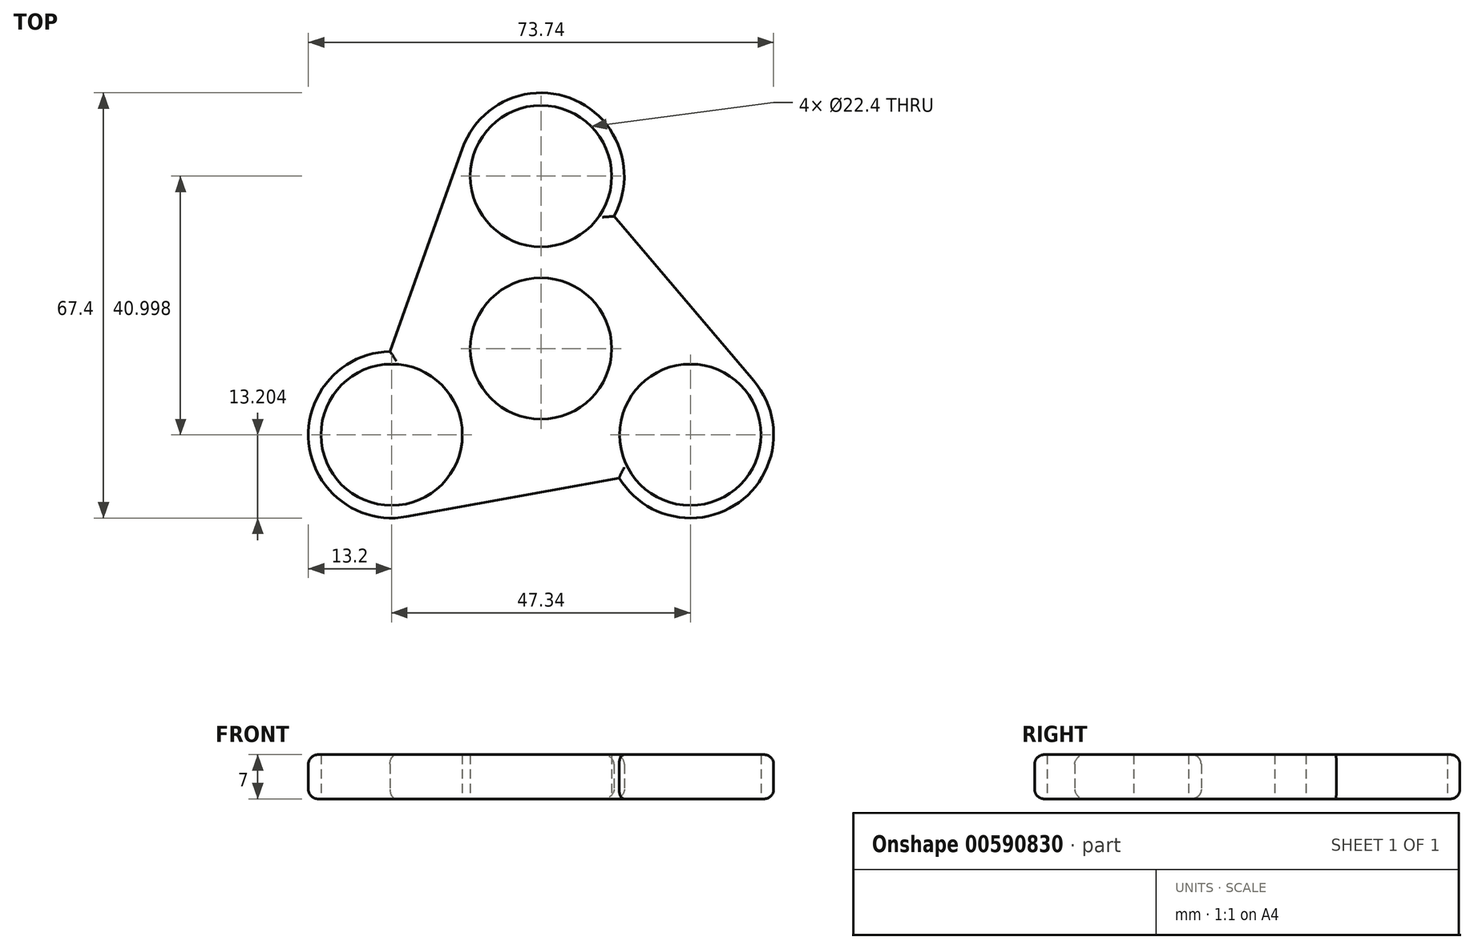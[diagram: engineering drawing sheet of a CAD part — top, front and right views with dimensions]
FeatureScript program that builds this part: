
annotation { "Feature Type Name" : "Feature", "Feature Type Description" : "" }
export const myFeature = defineFeature(function(context is Context, id is Id, definition is map)
    precondition{}
    {
        {
            var Q0;
            Q0=qCreatedBy(makeId("Top.planeOp"),FACE);
            var sketch = newSketch(context, id + "F0", { "sketchPlane" : qUnion([Q0])});
            skCircle(sketch, "E0", {"center": v(0, 0) * mm, "radius": 11.2 * mm});
            skCircle(sketch, "E1", {"center": v(0, 27.33) * mm, "radius": 11.2 * mm});
            skArc(sketch, "E2", {"start": v(11.57, 20.97) * mm, "mid": v(5.42, 39.37) * mm, "end": v(-12.43, 31.77) * mm});
            skCircle(sketch, "E3.1.0", {"center": v(-23.67, -13.67) * mm, "radius": 11.2 * mm});
            skArc(sketch, "E3.1.1", {"start": v(-23.95, -0.47) * mm, "mid": v(-36.8, -15) * mm, "end": v(-21.3, -26.65) * mm});
            skCircle(sketch, "E3.2.0", {"center": v(23.67, -13.67) * mm, "radius": 11.2 * mm});
            skArc(sketch, "E3.2.1", {"start": v(12.38, -20.5) * mm, "mid": v(31.39, -24.38) * mm, "end": v(33.73, -5.12) * mm});
            skLineSegment(sketch, "E4", {"start": v(11.57, 20.97) * mm, "end": v(33.73, -5.12) * mm});
            skLineSegment(sketch, "E5.1.0", {"start": v(-23.95, -0.47) * mm, "end": v(-12.43, 31.77) * mm});
            skLineSegment(sketch, "E5.2.0", {"start": v(12.38, -20.5) * mm, "end": v(-21.3, -26.65) * mm});
            skSolve(sketch);
        }
        {
            var Q0;
            Q0 = qSketchRegion(id + "F0", true);
            extrude(context, id + "F1", {"entities" : qUnion([Q0]), "depth" : 7 * mm, "offsetDistance" : 25 * mm});
        }
        {
            var Q0;
            Q0=makeQuery(id+"F1.opExtrude","CAP_EDGE",EDGE,{"disambiguationData":[OSD([sQuery(id+"F0.wireOp",EDGE,"E4")])],"isStart":false});
            var Q1;
            Q1=makeQuery(id+"F1.opExtrude","CAP_EDGE",EDGE,{"disambiguationData":[OSD([sQuery(id+"F0.wireOp",EDGE,"E3.2.1")])],"isStart":false});
            var Q2;
            Q2=makeQuery(id+"F1.opExtrude","CAP_EDGE",EDGE,{"disambiguationData":[OSD([sQuery(id+"F0.wireOp",EDGE,"E5.2.0")])],"isStart":false});
            var Q3;
            Q3=makeQuery(id+"F1.opExtrude","CAP_EDGE",EDGE,{"disambiguationData":[OSD([sQuery(id+"F0.wireOp",EDGE,"E3.1.1")])],"isStart":false});
            var Q4;
            Q4=makeQuery(id+"F1.opExtrude","CAP_EDGE",EDGE,{"disambiguationData":[OSD([sQuery(id+"F0.wireOp",EDGE,"E5.1.0")])],"isStart":false});
            var Q5;
            Q5=makeQuery(id+"F1.opExtrude","CAP_EDGE",EDGE,{"disambiguationData":[OSD([sQuery(id+"F0.wireOp",EDGE,"E2")])],"isStart":false});
            fillet(context, id + "F2", {"entities" : qUnion([Q0, Q1, Q2, Q3, Q4, Q5]), "radius" : 1.5 * mm, "tangentPropagation" : true, "allowEdgeOverflow" : false});
        }
        {
            var Q0;
            Q0=makeQuery(id+"F1.opExtrude","CAP_EDGE",EDGE,{"disambiguationData":[OSD([sQuery(id+"F0.wireOp",EDGE,"E3.2.1")])],"isStart":true});
            var Q1;
            Q1=makeQuery(id+"F1.opExtrude","CAP_EDGE",EDGE,{"disambiguationData":[OSD([sQuery(id+"F0.wireOp",EDGE,"E4")])],"isStart":true});
            var Q2;
            Q2=makeQuery(id+"F1.opExtrude","CAP_EDGE",EDGE,{"disambiguationData":[OSD([sQuery(id+"F0.wireOp",EDGE,"E2")])],"isStart":true});
            var Q3;
            Q3=makeQuery(id+"F1.opExtrude","CAP_EDGE",EDGE,{"disambiguationData":[OSD([sQuery(id+"F0.wireOp",EDGE,"E5.1.0")])],"isStart":true});
            var Q4;
            Q4=makeQuery(id+"F1.opExtrude","CAP_EDGE",EDGE,{"disambiguationData":[OSD([sQuery(id+"F0.wireOp",EDGE,"E3.1.1")])],"isStart":true});
            var Q5;
            Q5=makeQuery(id+"F1.opExtrude","CAP_EDGE",EDGE,{"disambiguationData":[OSD([sQuery(id+"F0.wireOp",EDGE,"E5.2.0")])],"isStart":true});
            fillet(context, id + "F3", {"entities" : qUnion([Q0, Q1, Q2, Q3, Q4, Q5]), "radius" : 1.5 * mm, "tangentPropagation" : true, "allowEdgeOverflow" : false});
        }
    });
